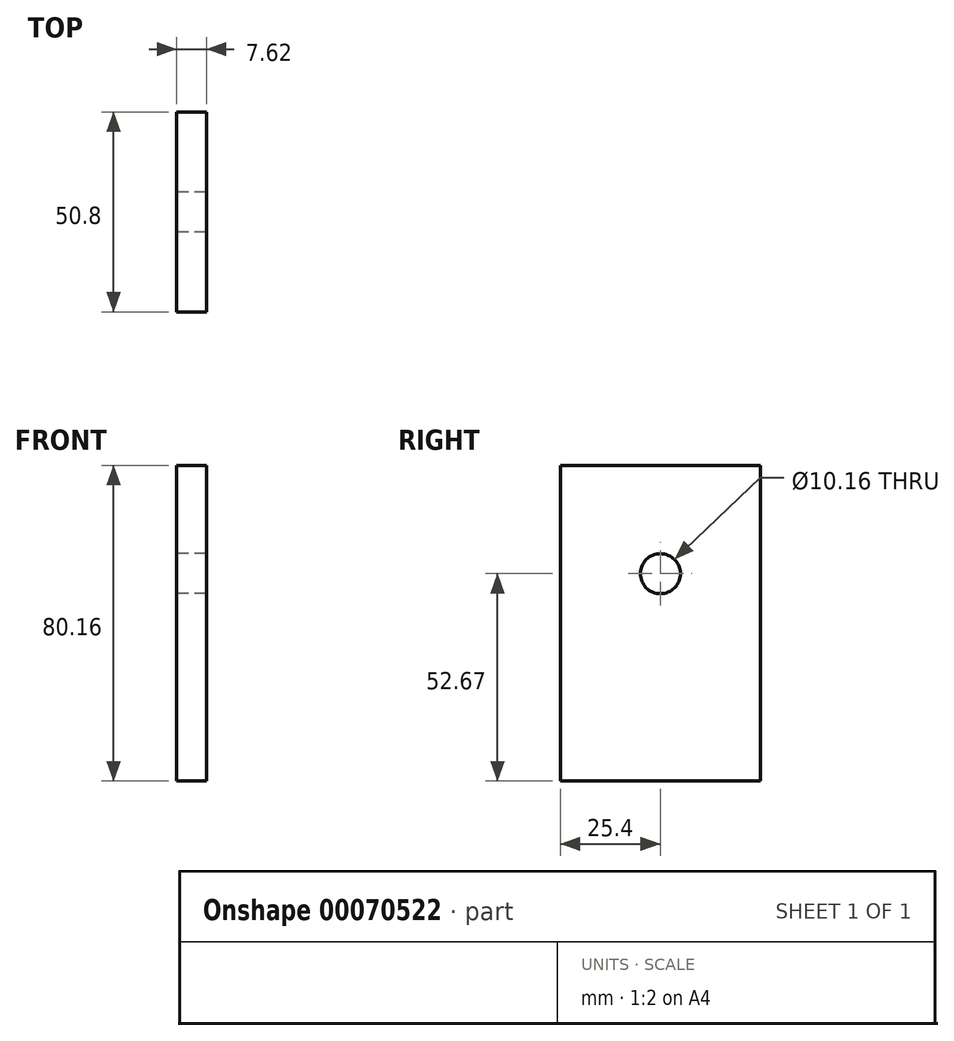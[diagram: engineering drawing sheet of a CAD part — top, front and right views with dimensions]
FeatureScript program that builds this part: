
annotation { "Feature Type Name" : "Feature", "Feature Type Description" : "" }
export const myFeature = defineFeature(function(context is Context, id is Id, definition is map)
    precondition{}
    {
        {
            var Q0;
            Q0=qCreatedBy(makeId("Right.planeOp"),FACE);
            var sketch = newSketch(context, id + "F0", { "sketchPlane" : qUnion([Q0])});
            skCircle(sketch, "E0", {"center": v(0, 0) * mm, "radius": 5.08 * mm});
            skLineSegment(sketch, "E1.bottom", {"start": v(0, 27.49) * mm, "end": v(25.4, 27.49) * mm});
            skLineSegment(sketch, "E1.top", {"start": v(0, -52.67) * mm, "end": v(25.4, -52.67) * mm});
            skLineSegment(sketch, "E1.left", {"start": v(0, 27.49) * mm, "end": v(0, -52.67) * mm});
            skLineSegment(sketch, "E1.right", {"start": v(25.4, 27.49) * mm, "end": v(25.4, -52.67) * mm});
            skLineSegment(sketch, "E2.MirrorCS", {"start": v(0, 27.49) * mm, "end": v(-25.4, 27.49) * mm});
            skLineSegment(sketch, "E3.MirrorCS", {"start": v(-25.4, 27.49) * mm, "end": v(-25.4, -52.67) * mm});
            skLineSegment(sketch, "E4.MirrorCS", {"start": v(0, -52.67) * mm, "end": v(-25.4, -52.67) * mm});
            skSolve(sketch);
        }
        {
            var Q0;
            {var subQ0=sQuery(id+"F0.wireOp",EDGE,"E2.MirrorCS");Q0=makeQuery(id+"F0.imprint","IMPRINT",FACE,{"disambiguationData":[TD([[makeQuery(id+"F0.imprint","IMPRINT",EDGE,{"derivedFrom":subQ0}),1.0]])]});}
            var Q1;
            {var subQ1=sQuery(id+"F0.wireOp",EDGE,"E1.bottom");Q1=makeQuery(id+"F0.imprint","IMPRINT",FACE,{"disambiguationData":[TD([[makeQuery(id+"F0.imprint","IMPRINT",EDGE,{"derivedFrom":subQ1}),-1.0]])]});}
            extrude(context, id + "F1", {"entities" : qUnion([Q0, Q1]), "depth" : 7.62 * mm});
        }
    });
